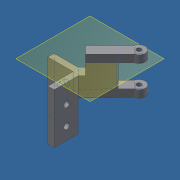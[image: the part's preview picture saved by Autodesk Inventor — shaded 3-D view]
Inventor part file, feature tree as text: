
AUTODESK INVENTOR PART (.ipt)
format: ipt  version: 2021 (Build 250183000, 183)  size: 167,424 bytes
history: native  units: mm
features: extrude x6, sketch x6, other x1, plane x1, projected_geometry x1
ambient origin geometry x8: Origin, YZ Plane, XZ Plane, XY Plane, X Axis, Y Axis, Z Axis, Center Point
bodies: Solid1 (feature_tree)
feature tree (15):
  other  "<userpath>\OneDrive\Objet3D\3DPrinter\Parameters.xlsx"
  extrude  "Extrusion1"  Depth=20.0mm
  plane  "Work Plane1"
  sketch  "Sketch3"  dims[d2=5.0mm d3=5.0mm]
  extrude  "Extrusion3"  Depth=5.0mm
  extrude  "Extrusion5"  Depth=30.0mm
  sketch  "Sketch8"  dims[d8=26.25mm d9=3.7mm]
  extrude  "Extrusion8"  Depth=3.7mm
  extrude  "Extrusion9"  Depth=25.0mm
  extrude  "Extrusion10"  Depth=5.0mm
  sketch  "Sketch1"  dims[d0=20.0mm d1=20.0mm]
  sketch  "Sketch5"  dims[d5=30.0mm d6=0.0mm d7=26.25mm]
  projected_geometry  "Projected Loop2"
  sketch  "Sketch9"  dims[d10=-6.0mm d13=25.0mm]
  sketch  "Sketch10"  dims[d16=18.0mm d17=0.0mm d18=5.0mm d19=135.0deg d22=25.0mm d23=0.0mm d40=4.5mm d41=10.0mm d42=10.0mm d43=4.5mm d44=10.0mm d45=15.0mm d46=10.0mm d47=10.0mm d48=10.0mm d49=15.0mm d50=4.5mm d51=4.5mm d52=20.0mm d53=0.0mm d54=20.0mm d55=0.0mm d56=135.0deg d57=0.0mm d58=15.0mm d59=0.0mm]
